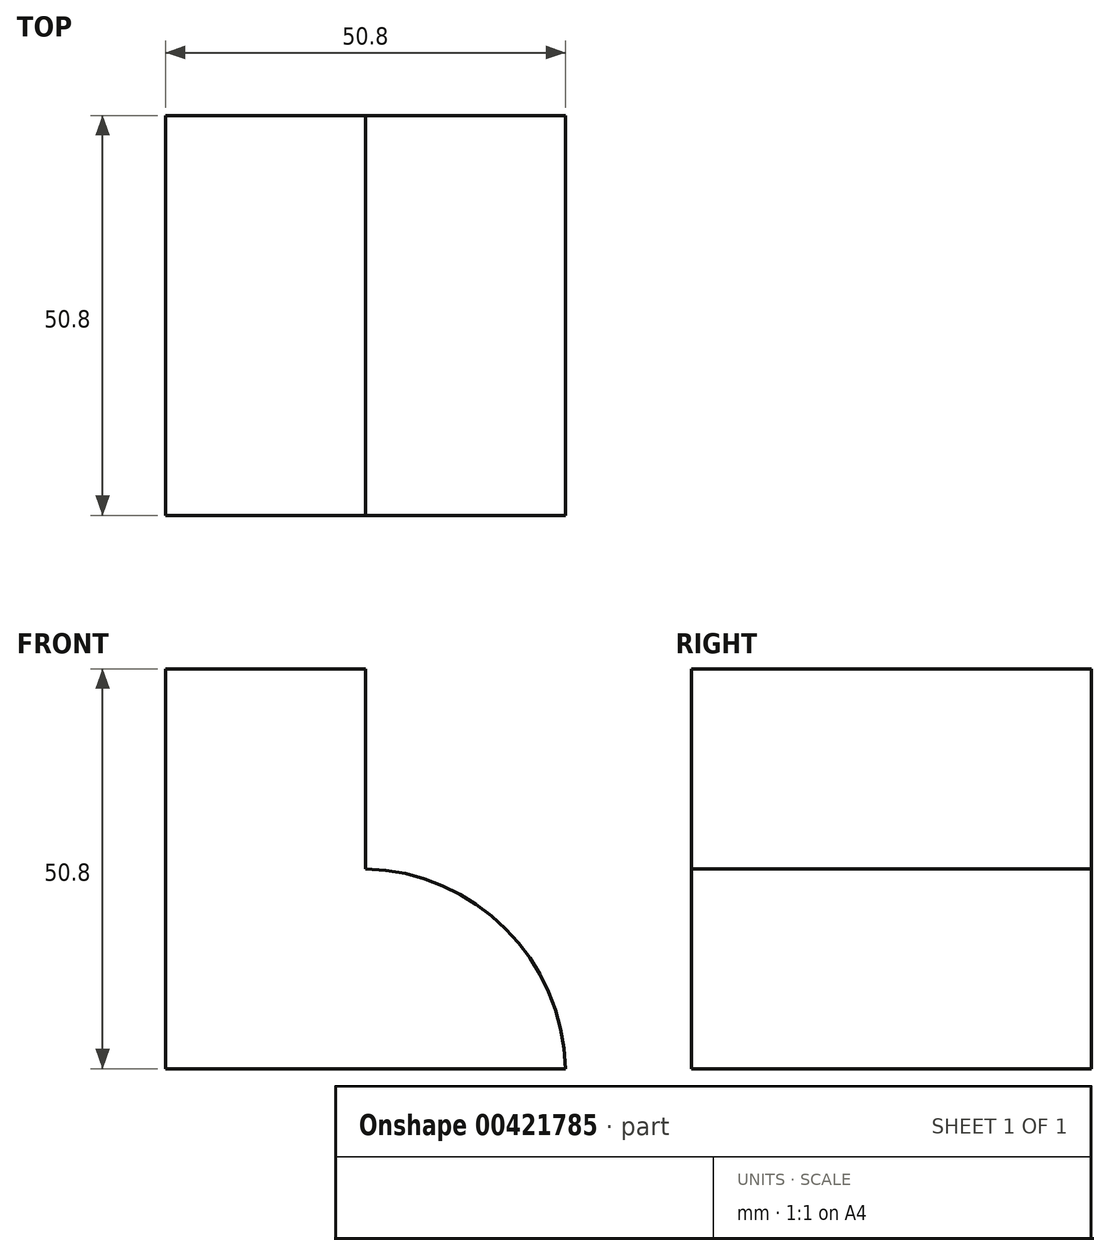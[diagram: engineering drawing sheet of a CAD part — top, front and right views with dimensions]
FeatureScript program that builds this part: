
annotation { "Feature Type Name" : "Feature", "Feature Type Description" : "" }
export const myFeature = defineFeature(function(context is Context, id is Id, definition is map)
    precondition{}
    {
        {
            var Q0;
            Q0=qCreatedBy(makeId("Front.planeOp"),FACE);
            var sketch = newSketch(context, id + "F0", { "sketchPlane" : qUnion([Q0])});
            skLineSegment(sketch, "E0", {"start": v(0, 0) * mm, "end": v(0, 50.8) * mm});
            skLineSegment(sketch, "E1", {"start": v(0, 0) * mm, "end": v(50.8, 0) * mm});
            skLineSegment(sketch, "E2", {"start": v(0, 50.8) * mm, "end": v(25.4, 50.8) * mm});
            skLineSegment(sketch, "E3", {"start": v(25.4, 50.8) * mm, "end": v(25.4, 25.4) * mm});
            skArc(sketch, "E4", {"start": v(50.8, 0) * mm, "mid": v(43.18, 17.78) * mm, "end": v(25.4, 25.4) * mm});
            skSolve(sketch);
        }
        {
            var Q0;
            Q0=makeQuery(id+"F0.imprint","IMPRINT",FACE,{"disambiguationData":[TD([[makeQuery(id+"F0.imprint","IMPRINT",EDGE,{"derivedFrom":sQuery(id+"F0.wireOp",EDGE,"E0")}),-1.0]])]});
            extrude(context, id + "F1", {"entities" : qUnion([Q0]), "depth" : 50.8 * mm});
        }
    });
